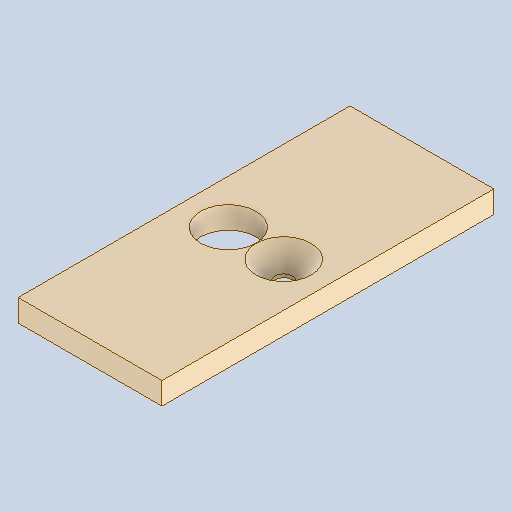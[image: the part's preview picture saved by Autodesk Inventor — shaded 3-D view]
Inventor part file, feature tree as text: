
AUTODESK INVENTOR PART (.ipt)
format: ipt  version: 2025 (Build 290162010, 162A)  size: 117,248 bytes
history: native  units: mm
features: other x4, reference x2, extrude x1, chamfer x1, sketch x1
ambient origin geometry x8: Origin, YZ Plane, XZ Plane, XY Plane, X Axis, Y Axis, Z Axis, Center Point
bodies: Volumenkörper1 (feature_tree)
feature tree (9):
  extrude  "Extrusion1"  Depth=2.0mm TaperAngle=45.0deg
  chamfer  "Fasen1"  [1 undecoded]
  sketch  "Skizze1"  dims[d0=2.0mm d1=0.0mm d2=1.7mm d3=2.0mm d4=45.0deg]
  reference  "Referenz1"
  reference  "Referenz2"
  other  "<userpath>\Documents\Inventor\Krandemonstrator\Demonstrator.iam"
  other  "Demonstrator.iam"
  other  "Katze_Lagerhalter_hinten:1"
  other  "LagerHH:1"
note: 1 required parameter value undecoded (feature->parameter linkage not recoverable at this tier; creation-order binding heuristic only, values carry confidence <= 0.55)
